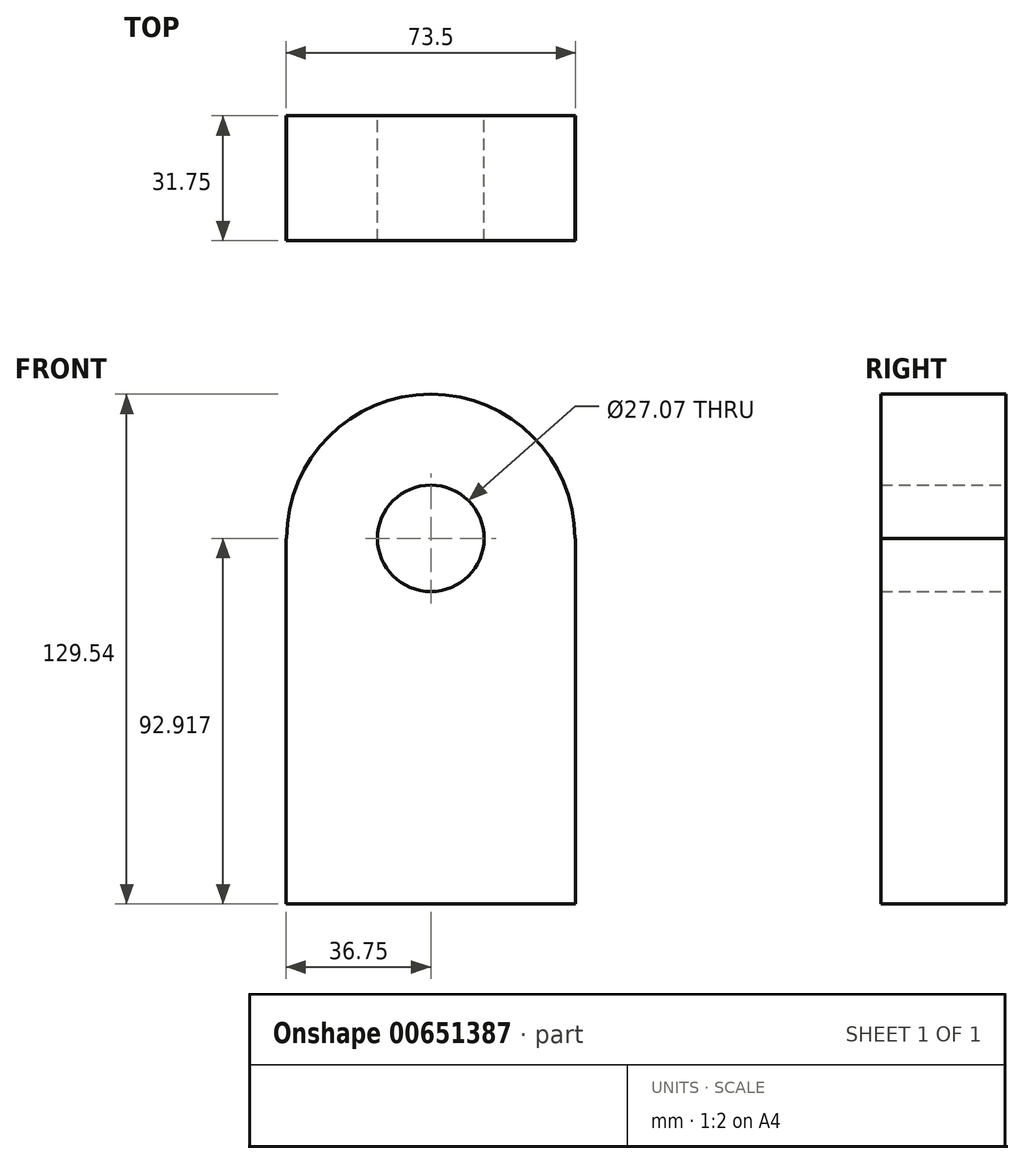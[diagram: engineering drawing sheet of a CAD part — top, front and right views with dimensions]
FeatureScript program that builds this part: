
annotation { "Feature Type Name" : "Feature", "Feature Type Description" : "" }
export const myFeature = defineFeature(function(context is Context, id is Id, definition is map)
    precondition{}
    {
        {
            var Q0;
            Q0=qCreatedBy(makeId("Front.planeOp"),FACE);
            var sketch = newSketch(context, id + "F0", { "sketchPlane" : qUnion([Q0])});
            skLineSegment(sketch, "E0.bottom", {"start": v(36.75, -46.46) * mm, "end": v(-36.75, -46.46) * mm});
            skLineSegment(sketch, "E0.top", {"start": v(36.75, 46.46) * mm, "end": v(-36.75, 46.46) * mm});
            skLineSegment(sketch, "E0.left", {"start": v(36.75, -46.46) * mm, "end": v(36.75, 46.46) * mm});
            skLineSegment(sketch, "E0.right", {"start": v(-36.75, -46.46) * mm, "end": v(-36.75, 46.46) * mm});
            skPoint(sketch, "E0.middle", {"position": v(0, 0) * mm});
            skArc(sketch, "E1", {"start": v(36.62, 46.46) * mm, "mid": v(0, 83.08) * mm, "end": v(-36.62, 46.46) * mm});
            skCircle(sketch, "E2", {"center": v(0, 46.46) * mm, "radius": 13.53 * mm});
            skSolve(sketch);
        }
        {
            var Q0;
            {var subQ0=sQuery(id+"F0.wireOp",EDGE,"E1");Q0=makeQuery(id+"F0.imprint","IMPRINT",FACE,{"disambiguationData":[TD([[makeQuery(id+"F0.imprint","IMPRINT",EDGE,{"derivedFrom":subQ0}),1.0]])]});}
            var Q1;
            Q1=makeQuery(id+"F0.imprint","IMPRINT",FACE,{"disambiguationData":[TD([[makeQuery(id+"F0.imprint","IMPRINT",EDGE,{"derivedFrom":sQuery(id+"F0.wireOp",EDGE,"E0.bottom")}),-1.0]])]});
            extrude(context, id + "F1", {"entities" : qUnion([Q0, Q1]), "depth" : 31.75 * mm, "offsetDistance" : 25.4 * mm});
        }
    });
